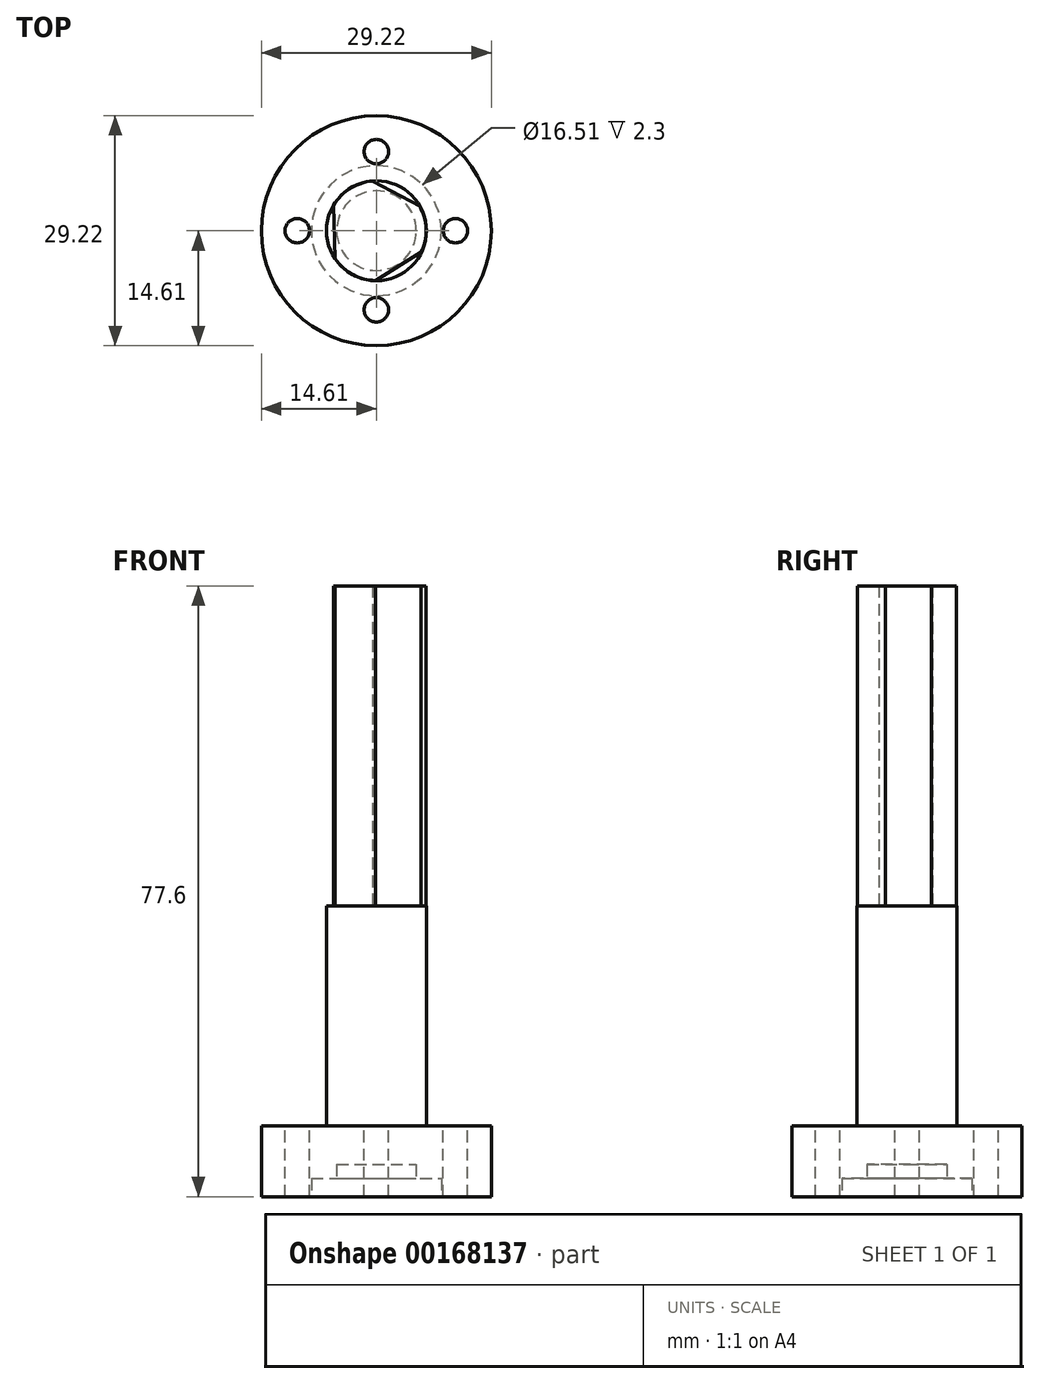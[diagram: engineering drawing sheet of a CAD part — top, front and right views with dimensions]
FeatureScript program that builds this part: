
annotation { "Feature Type Name" : "Feature", "Feature Type Description" : "" }
export const myFeature = defineFeature(function(context is Context, id is Id, definition is map)
    precondition{}
    {
        {
            var Q0;
            Q0=qCreatedBy(makeId("Top.planeOp"),FACE);
            var sketch = newSketch(context, id + "F0", { "sketchPlane" : qUnion([Q0])});
            skCircle(sketch, "E0", {"center": v(0, 0) * mm, "radius": 14.6 * mm});
            skSolve(sketch);
        }
        {
            var Q0;
            Q0=makeQuery(id+"F0.imprint","IMPRINT",FACE,{"disambiguationData":[TD([[makeQuery(id+"F0.imprint","IMPRINT",EDGE,{"derivedFrom":sQuery(id+"F0.wireOp",EDGE,"E0")}),1.0]])]});
            extrude(context, id + "F1", {"entities" : qUnion([Q0]), "depth" : 9.02 * mm});
        }
        {
            var Q0;
            Q0=makeQuery(id+"F1.opExtrude","CAP_FACE",FACE,{"disambiguationData":[OSD([sQuery(id+"F0.wireOp",EDGE,"E0")])],"isStart":false});
            var sketch = newSketch(context, id + "F2", { "sketchPlane" : qUnion([Q0])});
            skCircle(sketch, "E1", {"center": v(0, 0) * mm, "radius": 6.35 * mm});
            skSolve(sketch);
        }
        {
            var Q0;
            Q0 = qSketchRegion(id + "F2", true);
            extrude(context, id + "F3", {"entities" : qUnion([Q0]), "operationType" : NewBodyOperationType.ADD, "depth" : 27.94 * mm});
        }
        {
            var Q0;
            Q0=makeQuery(id+"F3.opExtrude","CAP_FACE",FACE,{"disambiguationData":[OSD([sQuery(id+"F2.wireOp",EDGE,"E1")])],"isStart":false});
            var sketch = newSketch(context, id + "F4", { "sketchPlane" : qUnion([Q0])});
            skCircle(sketch, "E2.cCircle", {"center": v(0, 0) * mm, "radius": 5.33 * mm, "construction": true});
            skLineSegment(sketch, "E2.0", {"start": v(10.66, 0.33) * mm, "end": v(-5.04, -9.4) * mm});
            skLineSegment(sketch, "E2.1", {"start": v(-5.04, -9.4) * mm, "end": v(-5.62, 9.07) * mm});
            skLineSegment(sketch, "E2.2", {"start": v(-5.62, 9.07) * mm, "end": v(10.66, 0.33) * mm});
            skPoint(sketch, "E2.0.midPoint", {"position": v(2.8, -4.53) * mm});
            skSolve(sketch);
        }
        {
            var Q0;
            Q0 = qSketchRegion(id + "F4", true);
            extrude(context, id + "F5", {"entities" : qUnion([Q0]), "operationType" : NewBodyOperationType.ADD, "depth" : 40.64 * mm});
        }
        {
            var Q0;
            Q0=makeQuery(id+"F1.opExtrude","CAP_FACE",FACE,{"disambiguationData":[OSD([sQuery(id+"F0.wireOp",EDGE,"E0")])],"isStart":true});
            var sketch = newSketch(context, id + "F6", { "sketchPlane" : qUnion([Q0])});
            skCircle(sketch, "E3", {"center": v(0, 0) * mm, "radius": 8.26 * mm});
            skSolve(sketch);
        }
        {
            var Q0;
            Q0 = qSketchRegion(id + "F6", true);
            extrude(context, id + "F7", {"entities" : qUnion([Q0]), "operationType" : NewBodyOperationType.REMOVE, "oppositeDirection" : true, "depth" : 2.3 * mm});
        }
        {
            var Q0;
            Q0=makeQuery(id+"F1.opExtrude","CAP_FACE",FACE,{"disambiguationData":[OSD([sQuery(id+"F0.wireOp",EDGE,"E0")])],"isStart":true});
            var sketch = newSketch(context, id + "F8", { "sketchPlane" : qUnion([Q0])});
            skCircle(sketch, "E4", {"center": v(0, 0) * mm, "radius": 5.06 * mm});
            skSolve(sketch);
        }
        {
            var Q0;
            Q0 = qSketchRegion(id + "F8", true);
            extrude(context, id + "F9", {"entities" : qUnion([Q0]), "operationType" : NewBodyOperationType.REMOVE, "oppositeDirection" : true, "depth" : 4.1 * mm});
        }
        {
            var Q0;
            Q0=makeQuery(id+"F1.opExtrude","CAP_FACE",FACE,{"disambiguationData":[OSD([sQuery(id+"F0.wireOp",EDGE,"E0")])],"isStart":false});
            var sketch = newSketch(context, id + "F10", { "sketchPlane" : qUnion([Q0])});
            skPoint(sketch, "E5", {"position": v(-10.05, 0) * mm});
            skPoint(sketch, "E6", {"position": v(0, 10.05) * mm});
            skPoint(sketch, "E7", {"position": v(10.05, 0) * mm});
            skPoint(sketch, "E8", {"position": v(0, -10.05) * mm});
            skCircle(sketch, "E9", {"center": v(0, 0) * mm, "radius": 10.05 * mm, "construction": true});
            skSolve(sketch);
        }
        {
            var Q0;
            Q0=sQuery(id+"F10.wireOp",VERTEX,"E8");
            var Q1;
            Q1=sQuery(id+"F10.wireOp",VERTEX,"E5");
            var Q2;
            Q2=sQuery(id+"F10.wireOp",VERTEX,"E6");
            var Q3;
            Q3=sQuery(id+"F10.wireOp",VERTEX,"E7");
            var Q4;
            Q4=makeQuery(id+"F1.opExtrude","SWEPT_BODY",BODY,{"disambiguationData":[OSD([sQuery(id+"F0.wireOp",EDGE,"E0")])]});
            hole(context, id + "F11", {"style" : HoleStyle.SIMPLE, "endStyle" : HoleEndStyle.THROUGH, "holeDiameter" : 3.1 * mm, "locations" : qUnion([Q0, Q1, Q2, Q3]), "scope" : qUnion([Q4]), "isTappedThrough" : true});
        }
        {
            var Q0;
            {var subQ0=sQuery(id+"F2.wireOp",EDGE,"E1");var subQ1=sQuery(id+"F4.wireOp",EDGE,"E2.0");Q0=makeQuery(id+"F5.boolean.opBoolean","SPLIT",FACE,{"disambiguationData":[TD([makeQuery(id+"F5.opExtrude","SWEPT_FACE",FACE,{"disambiguationData":[OSD([subQ1])]})])],"derivedFrom":makeQuery(id+"F3.opExtrude","CAP_FACE",FACE,{"disambiguationData":[OSD([subQ0])],"isStart":false})});}
            var sketch = newSketch(context, id + "F12", { "sketchPlane" : qUnion([Q0])});
            skCircle(sketch, "E10", {"center": v(0, 0) * mm, "radius": 6.32 * mm});
            skCircle(sketch, "E11", {"center": v(0, 0) * mm, "radius": 15.65 * mm});
            skSolve(sketch);
        }
        {
            var Q0;
            Q0 = qSketchRegion(id + "F12", true);
            extrude(context, id + "F13", {"entities" : qUnion([Q0]), "operationType" : NewBodyOperationType.REMOVE, "endBound" : BoundingType.THROUGH_ALL, "depth" : 25.4 * mm});
        }
    });
